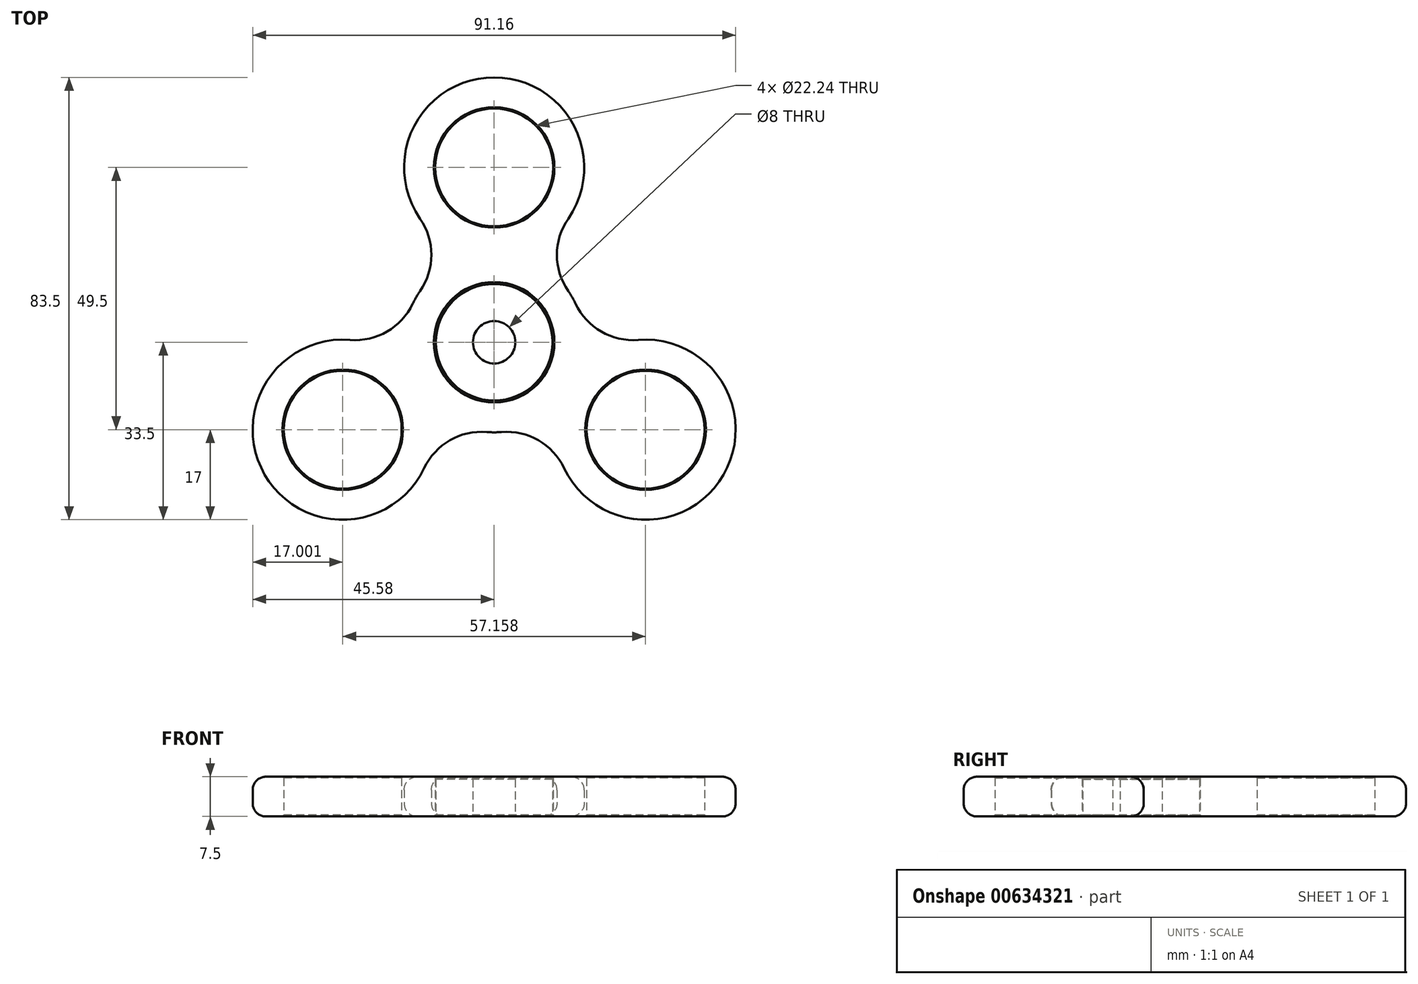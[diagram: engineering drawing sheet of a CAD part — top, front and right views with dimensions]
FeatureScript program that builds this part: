
annotation { "Feature Type Name" : "Feature", "Feature Type Description" : "" }
export const myFeature = defineFeature(function(context is Context, id is Id, definition is map)
    precondition{}
    {
        {
            var Q0;
            Q0=qCreatedBy(makeId("Top.planeOp"),FACE);
            var sketch = newSketch(context, id + "F0", { "sketchPlane" : qUnion([Q0])});
            skCircle(sketch, "E0", {"center": v(0, 0) * mm, "radius": 4 * mm});
            skCircle(sketch, "E1", {"center": v(0, 0) * mm, "radius": 11 * mm});
            skSolve(sketch);
        }
        {
            var Q0;
            Q0=makeQuery(id+"F0.imprint","IMPRINT",FACE,{"disambiguationData":[TD([[makeQuery(id+"F0.imprint","IMPRINT",EDGE,{"derivedFrom":sQuery(id+"F0.wireOp",EDGE,"E0")}),-1.0]])]});
            extrude(context, id + "F1", {"entities" : qUnion([Q0]), "depth" : 7 * mm, "offsetDistance" : 25 * mm});
        }
        {
            var Q0;
            Q0=qCreatedBy(makeId("Top.planeOp"),FACE);
            var sketch = newSketch(context, id + "F2", { "sketchPlane" : qUnion([Q0])});
            skArc(sketch, "E2.0", {"start": v(-1.39, -16.94) * mm, "mid": v(0, -17) * mm, "end": v(1.39, -16.94) * mm});
            skCircle(sketch, "E3.0", {"center": v(0, 0) * mm, "radius": 11.12 * mm});
            skArc(sketch, "E4", {"start": v(13.98, 23.33) * mm, "mid": v(0, 50) * mm, "end": v(-13.98, 23.33) * mm});
            skCircle(sketch, "E5", {"center": v(0, 33) * mm, "radius": 11.12 * mm});
            skArc(sketch, "E6.1.0", {"start": v(-27.2, 0.44) * mm, "mid": v(-43.3, -25) * mm, "end": v(-13.21, -23.77) * mm});
            skCircle(sketch, "E6.1.1", {"center": v(-28.58, -16.5) * mm, "radius": 11.12 * mm});
            skArc(sketch, "E6.2.0", {"start": v(13.21, -23.77) * mm, "mid": v(43.3, -25) * mm, "end": v(27.2, 0.44) * mm});
            skCircle(sketch, "E6.2.1", {"center": v(28.58, -16.5) * mm, "radius": 11.12 * mm});
            skArc(sketch, "E7.trimOffspring", {"start": v(-13.98, 9.67) * mm, "mid": v(-14.72, 8.5) * mm, "end": v(-15.37, 7.27) * mm});
            skArc(sketch, "E8.trimOffspring", {"start": v(15.37, 7.27) * mm, "mid": v(14.72, 8.5) * mm, "end": v(13.98, 9.67) * mm});
            skPoint(sketch, "E9.visualSharp", {"position": v(-4.1, 16.5) * mm});
            skArc(sketch, "E9.filletArc", {"start": v(-13.98, 9.67) * mm, "mid": v(-11.85, 16.5) * mm, "end": v(-13.98, 23.33) * mm});
            skPoint(sketch, "E10.visualSharp", {"position": v(4.1, 16.5) * mm});
            skArc(sketch, "E10.filletArc", {"start": v(13.98, 23.33) * mm, "mid": v(11.85, 16.5) * mm, "end": v(13.98, 9.67) * mm});
            skPoint(sketch, "E11.visualSharp", {"position": v(16.34, -4.7) * mm});
            skArc(sketch, "E11.filletArc", {"start": v(15.37, 7.27) * mm, "mid": v(20.21, 2.01) * mm, "end": v(27.2, 0.44) * mm});
            skPoint(sketch, "E12.visualSharp", {"position": v(12.24, -11.8) * mm});
            skArc(sketch, "E12.filletArc", {"start": v(13.21, -23.77) * mm, "mid": v(8.37, -18.51) * mm, "end": v(1.39, -16.94) * mm});
            skPoint(sketch, "E13.visualSharp", {"position": v(-12.24, -11.8) * mm});
            skArc(sketch, "E13.filletArc", {"start": v(-1.39, -16.94) * mm, "mid": v(-8.37, -18.51) * mm, "end": v(-13.21, -23.77) * mm});
            skPoint(sketch, "E14.visualSharp", {"position": v(-16.34, -4.7) * mm});
            skArc(sketch, "E14.filletArc", {"start": v(-27.2, 0.44) * mm, "mid": v(-20.21, 2.01) * mm, "end": v(-15.37, 7.27) * mm});
            skSolve(sketch);
        }
        {
            var Q0;
            Q0=makeQuery(id+"F2.imprint","IMPRINT",FACE,{"disambiguationData":[TD([[makeQuery(id+"F2.imprint","IMPRINT",EDGE,{"derivedFrom":sQuery(id+"F2.wireOp",EDGE,"E2.0")}),1.0]])]});
            extrude(context, id + "F3", {"entities" : qUnion([Q0]), "depth" : 7.5 * mm, "offsetDistance" : 25 * mm});
        }
        {
            var Q0;
            Q0=makeQuery(id+"F3.opExtrude","CAP_EDGE",EDGE,{"disambiguationData":[OSD([sQuery(id+"F2.wireOp",EDGE,"E13.filletArc")])],"isStart":false});
            var Q1;
            Q1=makeQuery(id+"F3.opExtrude","CAP_EDGE",EDGE,{"disambiguationData":[OSD([sQuery(id+"F2.wireOp",EDGE,"E4")])],"isStart":true});
            fillet(context, id + "F4", {"entities" : qUnion([Q0, Q1]), "radius" : 2.5 * mm, "tangentPropagation" : true, "allowEdgeOverflow" : false});
        }
        {
            var Q0;
            Q0=makeQuery(id+"F3.opExtrude","CAP_EDGE",EDGE,{"disambiguationData":[OSD([sQuery(id+"F2.wireOp",EDGE,"E6.1.1")])],"isStart":true});
            var Q1;
            Q1=makeQuery(id+"F3.opExtrude","CAP_EDGE",EDGE,{"disambiguationData":[OSD([sQuery(id+"F2.wireOp",EDGE,"E5")])],"isStart":true});
            var Q2;
            Q2=makeQuery(id+"F3.opExtrude","CAP_EDGE",EDGE,{"disambiguationData":[OSD([sQuery(id+"F2.wireOp",EDGE,"E6.2.1")])],"isStart":true});
            var Q3;
            Q3=makeQuery(id+"F3.opExtrude","CAP_EDGE",EDGE,{"disambiguationData":[OSD([sQuery(id+"F2.wireOp",EDGE,"E6.2.1")])],"isStart":false});
            var Q4;
            Q4=makeQuery(id+"F3.opExtrude","CAP_EDGE",EDGE,{"disambiguationData":[OSD([sQuery(id+"F2.wireOp",EDGE,"E6.1.1")])],"isStart":false});
            var Q5;
            Q5=makeQuery(id+"F3.opExtrude","CAP_EDGE",EDGE,{"disambiguationData":[OSD([sQuery(id+"F2.wireOp",EDGE,"E5")])],"isStart":false});
            var Q6;
            Q6=makeQuery(id+"F3.opExtrude","CAP_EDGE",EDGE,{"disambiguationData":[OSD([sQuery(id+"F2.wireOp",EDGE,"E3.0")])],"isStart":false});
            var Q7;
            Q7=makeQuery(id+"F3.opExtrude","CAP_EDGE",EDGE,{"disambiguationData":[OSD([sQuery(id+"F2.wireOp",EDGE,"E3.0")])],"isStart":true});
            chamfer(context, id + "F5", {"entities" : qUnion([Q0, Q1, Q2, Q3, Q4, Q5, Q6, Q7]), "width" : .25 * mm, "tangentPropagation" : true});
        }
    });
